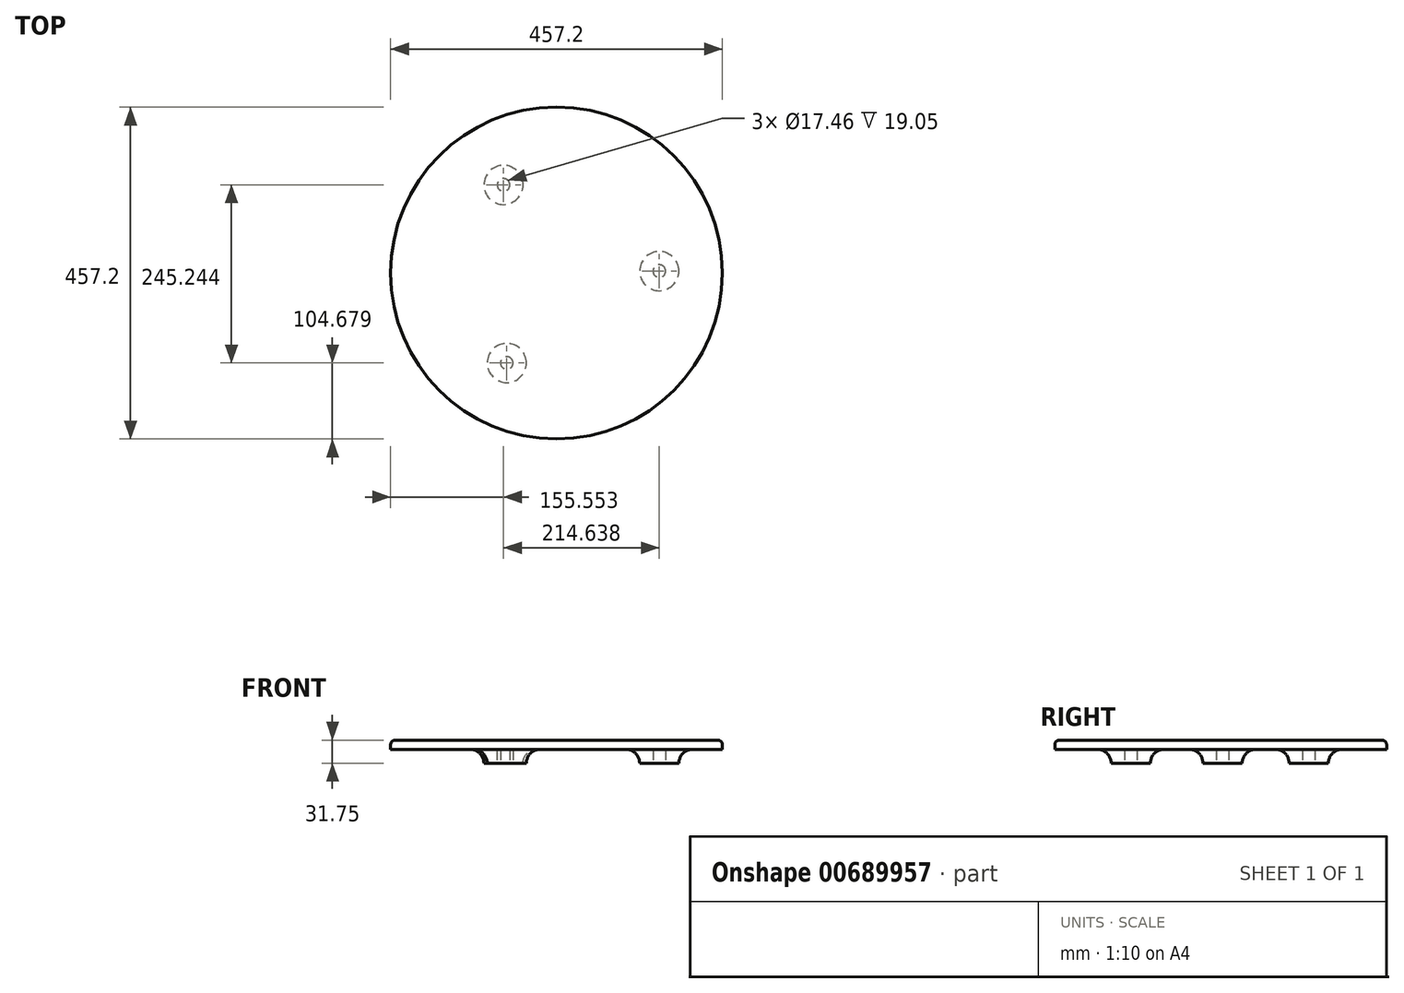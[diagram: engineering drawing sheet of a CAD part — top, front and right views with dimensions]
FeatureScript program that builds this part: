
annotation { "Feature Type Name" : "Feature", "Feature Type Description" : "" }
export const myFeature = defineFeature(function(context is Context, id is Id, definition is map)
    precondition{}
    {
        {
            var Q0;
            Q0=qCreatedBy(makeId("Top.planeOp"),FACE);
            var sketch = newSketch(context, id + "F0", { "sketchPlane" : qUnion([Q0])});
            skEllipse(sketch, "E0", {"center": v(0, 0) * mm, "majorRadius": 228.6 * mm, "minorRadius": 228.6 * mm, "majorAxis": v(0, -1)});
            skSolve(sketch);
        }
        {
            var Q0;
            Q0=makeQuery(id+"F0.imprint","IMPRINT",FACE,{"disambiguationData":[TD([[makeQuery(id+"F0.imprint","IMPRINT",EDGE,{"derivedFrom":sQuery(id+"F0.wireOp",EDGE,"E0")}),1.0]])]});
            extrude(context, id + "F1", {"entities" : qUnion([Q0]), "depth" : 31.75 * mm, "offsetDistance" : 25.4 * mm});
        }
        {
            var Q0;
            Q0=makeQuery(id+"F1.opExtrude","CAP_FACE",FACE,{"disambiguationData":[OSD([sQuery(id+"F0.wireOp",EDGE,"E0")])],"isStart":true});
            var sketch = newSketch(context, id + "F2", { "sketchPlane" : qUnion([Q0])});
            skCircle(sketch, "E1.cCircle", {"center": v(0, 0) * mm, "radius": 141.62 * mm, "construction": true});
            skLineSegment(sketch, "E1.0", {"start": v(-68.55, 123.92) * mm, "end": v(141.6, -2.6) * mm});
            skLineSegment(sketch, "E1.1", {"start": v(141.6, -2.6) * mm, "end": v(-73.05, -121.32) * mm});
            skLineSegment(sketch, "E1.2", {"start": v(-73.05, -121.32) * mm, "end": v(-68.55, 123.92) * mm});
            skCircle(sketch, "E2", {"center": v(-68.55, 123.92) * mm, "radius": 26.99 * mm});
            skCircle(sketch, "E3", {"center": v(-73.05, -121.32) * mm, "radius": 26.99 * mm});
            skCircle(sketch, "E4", {"center": v(141.6, -2.6) * mm, "radius": 26.99 * mm});
            skSolve(sketch);
        }
        {
            var Q0;
            Q0=makeQuery(id+"F2.imprint","IMPRINT",FACE,{"disambiguationData":[TD([[makeQuery(id+"F2.imprint","IMPRINT",EDGE,{"derivedFrom":makeQuery(id+"F1.opExtrude","CAP_EDGE",EDGE,{"disambiguationData":[OSD([sQuery(id+"F0.wireOp",EDGE,"E0")])],"isStart":true})}),-1.0]])]});
            var Q1;
            {var subQ3=sQuery(id+"F2.wireOp",EDGE,"E2");var subQ5=sQuery(id+"F2.wireOp",EDGE,"E1.0");var subQ6=makeQuery(id+"F2.imprint","INTERSECT",VERTEX,{"derivedFrom":[subQ5,subQ3]});Q1=makeQuery(id+"F2.imprint","IMPRINT",FACE,{"disambiguationData":[TD([[makeQuery(id+"F2.imprint","IMPRINT",EDGE,{"disambiguationData":[TD([[subQ6,-1.0]])],"derivedFrom":subQ5}),-1.0]])]});}
            extrude(context, id + "F3", {"entities" : qUnion([Q0, Q1]), "operationType" : NewBodyOperationType.REMOVE, "oppositeDirection" : true, "depth" : 19.05 * mm, "offsetDistance" : 25.4 * mm});
        }
        {
            var Q0;
            Q0=makeQuery(id+"F3.boolean.opBoolean","COPY",EDGE,{"derivedFrom":makeQuery(id+"F3.opExtrude","CAP_EDGE",EDGE,{"disambiguationData":[OSD([sQuery(id+"F2.wireOp",EDGE,"E2")])],"isStart":false})});
            var Q1;
            Q1=makeQuery(id+"F3.boolean.opBoolean","COPY",EDGE,{"derivedFrom":makeQuery(id+"F3.opExtrude","CAP_EDGE",EDGE,{"disambiguationData":[OSD([sQuery(id+"F2.wireOp",EDGE,"E4")])],"isStart":false})});
            var Q2;
            Q2=makeQuery(id+"F3.boolean.opBoolean","COPY",EDGE,{"derivedFrom":makeQuery(id+"F3.opExtrude","CAP_EDGE",EDGE,{"disambiguationData":[OSD([sQuery(id+"F2.wireOp",EDGE,"E3")])],"isStart":false})});
            fillet(context, id + "F4", {"entities" : qUnion([Q0, Q1, Q2]), "radius" : 19.05 * mm, "tangentPropagation" : true, "allowEdgeOverflow" : false});
        }
        {
            var Q0;
            Q0=makeQuery(id+"F1.opExtrude","CAP_EDGE",EDGE,{"disambiguationData":[OSD([sQuery(id+"F0.wireOp",EDGE,"E0")])],"isStart":false});
            var Q1;
            Q1=makeQuery(id+"F3.boolean.opBoolean","COPY",EDGE,{"derivedFrom":makeQuery(id+"F3.opExtrude","CAP_EDGE",EDGE,{"disambiguationData":[OSD([sQuery(id+"F0.wireOp",EDGE,"E0")])],"isStart":false})});
            fillet(context, id + "F5", {"entities" : qUnion([Q0, Q1]), "radius" : 6.35 * mm, "tangentPropagation" : true, "allowEdgeOverflow" : false});
        }
        {
            var Q0;
            Q0=makeQuery(id+"F3.boolean.opBoolean","SPLIT",FACE,{"disambiguationData":[TD([makeQuery(id+"F3.opExtrude","SWEPT_FACE",FACE,{"disambiguationData":[OSD([sQuery(id+"F2.wireOp",EDGE,"E2")])]})])],"derivedFrom":makeQuery(id+"F1.opExtrude","CAP_FACE",FACE,{"disambiguationData":[OSD([sQuery(id+"F0.wireOp",EDGE,"E0")])],"isStart":true})});
            var sketch = newSketch(context, id + "F6", { "sketchPlane" : qUnion([Q0])});
            skCircle(sketch, "E5", {"center": v(-68.55, 123.92) * mm, "radius": 8.73 * mm});
            skSolve(sketch);
        }
        {
            var Q0;
            Q0=makeQuery(id+"F3.boolean.opBoolean","SPLIT",FACE,{"disambiguationData":[TD([makeQuery(id+"F3.opExtrude","SWEPT_FACE",FACE,{"disambiguationData":[OSD([sQuery(id+"F2.wireOp",EDGE,"E4")])]})])],"derivedFrom":makeQuery(id+"F1.opExtrude","CAP_FACE",FACE,{"disambiguationData":[OSD([sQuery(id+"F0.wireOp",EDGE,"E0")])],"isStart":true})});
            var sketch = newSketch(context, id + "F7", { "sketchPlane" : qUnion([Q0])});
            skCircle(sketch, "E6", {"center": v(141.6, -2.6) * mm, "radius": 8.73 * mm});
            skSolve(sketch);
        }
        {
            var Q0;
            Q0=makeQuery(id+"F3.boolean.opBoolean","SPLIT",FACE,{"disambiguationData":[TD([makeQuery(id+"F3.opExtrude","SWEPT_FACE",FACE,{"disambiguationData":[OSD([sQuery(id+"F2.wireOp",EDGE,"E3")])]})])],"derivedFrom":makeQuery(id+"F1.opExtrude","CAP_FACE",FACE,{"disambiguationData":[OSD([sQuery(id+"F0.wireOp",EDGE,"E0")])],"isStart":true})});
            var sketch = newSketch(context, id + "F8", { "sketchPlane" : qUnion([Q0])});
            skCircle(sketch, "E7", {"center": v(-73.05, -121.32) * mm, "radius": 8.73 * mm});
            skSolve(sketch);
        }
        {
            var Q0;
            Q0=makeQuery(id+"F6.imprint","IMPRINT",FACE,{"disambiguationData":[TD([[makeQuery(id+"F6.imprint","IMPRINT",EDGE,{"derivedFrom":sQuery(id+"F6.wireOp",EDGE,"E5")}),1.0]])]});
            var Q1;
            Q1=makeQuery(id+"F7.imprint","IMPRINT",FACE,{"disambiguationData":[TD([[makeQuery(id+"F7.imprint","IMPRINT",EDGE,{"derivedFrom":sQuery(id+"F7.wireOp",EDGE,"E6")}),1.0]])]});
            var Q2;
            Q2=makeQuery(id+"F8.imprint","IMPRINT",FACE,{"disambiguationData":[TD([[makeQuery(id+"F8.imprint","IMPRINT",EDGE,{"derivedFrom":sQuery(id+"F8.wireOp",EDGE,"E7")}),1.0]])]});
            extrude(context, id + "F9", {"entities" : qUnion([Q0, Q1, Q2]), "operationType" : NewBodyOperationType.REMOVE, "oppositeDirection" : true, "depth" : 19.05 * mm, "offsetDistance" : 25.4 * mm});
        }
    });
